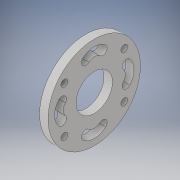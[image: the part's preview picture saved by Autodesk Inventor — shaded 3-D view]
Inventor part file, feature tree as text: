
AUTODESK INVENTOR PART (.ipt)
format: ipt  version: 2019 (Build 230136000, 136)  size: 173,056 bytes
history: native  units: mm
features: sketch x4, extrude x3, pattern_circular x1, projected_geometry x1
ambient origin geometry x8: Origin, YZ Plane, XZ Plane, XY Plane, X Axis, Y Axis, Z Axis, Center Point
bodies: Body1 (feature_tree)
feature tree (9):
  extrude  "Extrusion4"  Depth=10.0mm
  extrude  "Extrusion5"  Depth=10.0mm TaperAngle=360.0deg
  pattern_circular  "Circular Pattern2"  [2 undecoded]
  sketch  "Sketch5"  dims[d38=10.0mm d39=0.0mm]
  extrude  "Extrusion6"  [1 undecoded]
  sketch  "Sketch2"  dims[d23=10.0mm d24=0.0mm d28=15.0mm]
  sketch  "Sketch4"  dims[d29=10.0mm d30=0.0mm d31=40.0mm d32=360.0deg]
  projected_geometry  "Projected Loop1"
  sketch  "Sketch6"
note: 3 required parameter values undecoded (feature->parameter linkage not recoverable at this tier; creation-order binding heuristic only, values carry confidence <= 0.55)
